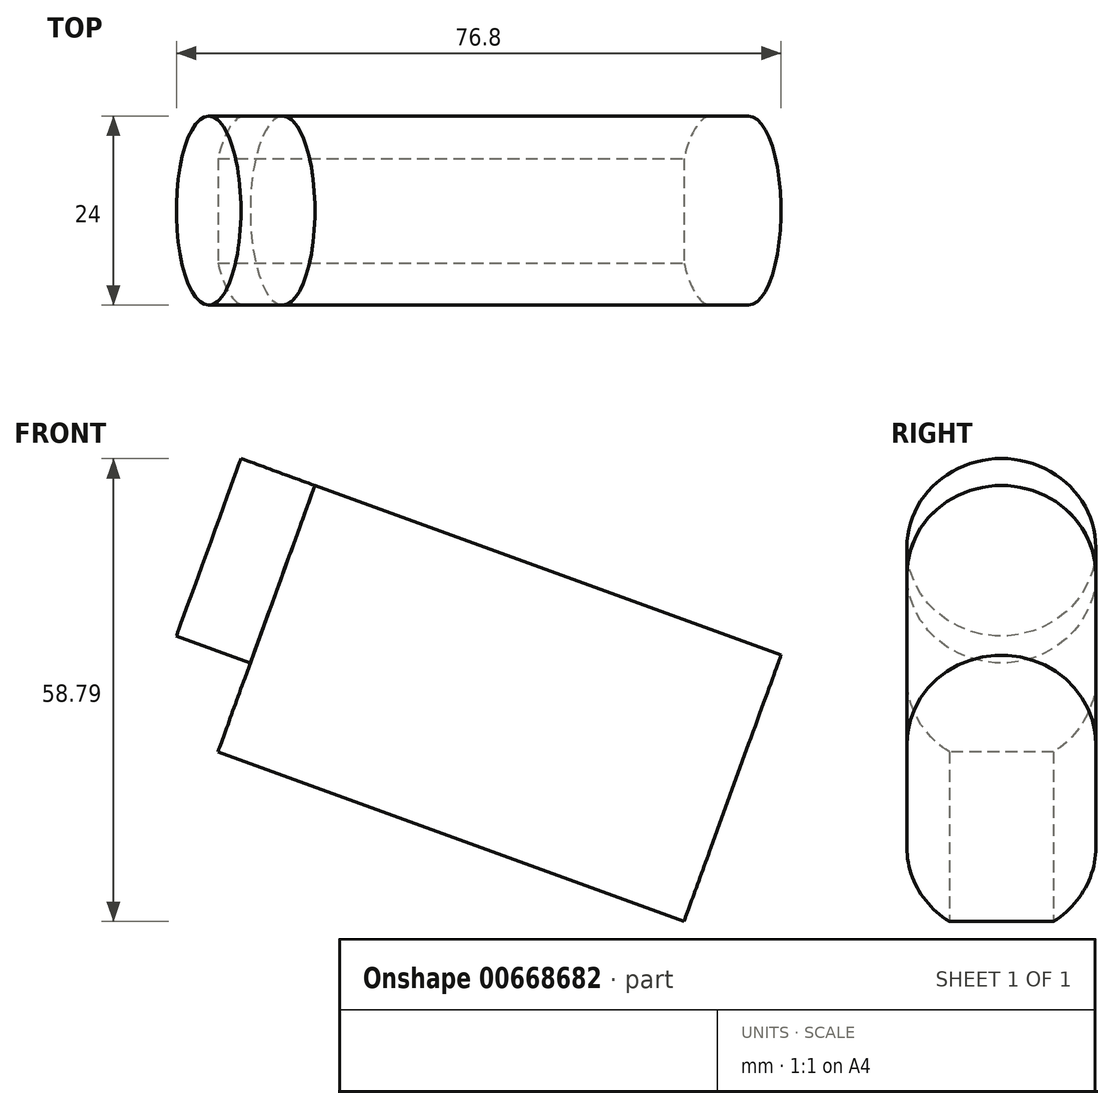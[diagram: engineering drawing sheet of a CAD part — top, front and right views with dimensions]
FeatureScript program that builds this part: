
annotation { "Feature Type Name" : "Feature", "Feature Type Description" : "" }
export const myFeature = defineFeature(function(context is Context, id is Id, definition is map)
    precondition{}
    {
        {
            var Q0;
            Q0=qCreatedBy(makeId("Right.planeOp"),FACE);
            var sketch = newSketch(context, id + "F0", { "sketchPlane" : qUnion([Q0])});
            skLineSegment(sketch, "E0", {"start": v(-93.73, 0) * mm, "end": v(85.96, 0) * mm, "construction": true});
            skSolve(sketch);
        }
        {
            var Q0;
            Q0=qCreatedBy(makeId("Right.planeOp"),FACE);
            var Q1;
            Q1=sQuery(id+"F0.wireOp",EDGE,"E0");
            cPlane(context, id + "F1", {"entities" : qUnion([Q0, Q1]), "cplaneType" : CPlaneType.LINE_ANGLE, "offset" : 25 * mm, "angle" : 20 * degree, "width" : 150 * mm, "height" : 150 * mm});
        }
        {
            var Q0;
            Q0=qCreatedBy(makeId("Top.planeOp"),FACE);
            var sketch = newSketch(context, id + "F2", { "sketchPlane" : qUnion([Q0])});
            skFitSpline(sketch, "E1", {"points": [v(-76, 0) * mm, v(-46.58, 16.57) * mm, v(0, 13) * mm, v(74, 0) * mm], "startDerivative": vector(0.2, 174.07) * mm, "endDerivative": vector(331.92, -62.8) * mm});
            skFitSpline(sketch, "E2.MirrorCS", {"points": [v(-76, 0) * mm, v(-46.58, -16.57) * mm, v(0, -13) * mm, v(74, 0) * mm], "startDerivative": vector(0.2, -174.07) * mm, "endDerivative": vector(331.92, 62.8) * mm});
            skLineSegment(sketch, "E3", {"start": v(-166.1, 0) * mm, "end": v(172.43, 0) * mm, "construction": true});
            skSolve(sketch);
        }
        {
            var Q0;
            Q0=qCreatedBy(id+"F1.planeOp",FACE);
            var sketch = newSketch(context, id + "F3", { "sketchPlane" : qUnion([Q0])});
            skCircle(sketch, "E4", {"center": v(0, 0) * mm, "radius": 12 * mm});
            skArc(sketch, "E5", {"start": v(-12, -14) * mm, "mid": v(-10.57, -19.67) * mm, "end": v(-6.63, -24) * mm});
            skLineSegment(sketch, "E6", {"start": v(-12, 0) * mm, "end": v(-12, -14) * mm});
            skLineSegment(sketch, "E7", {"start": v(12, 0) * mm, "end": v(12, -14) * mm});
            skLineSegment(sketch, "E8", {"start": v(-6.63, -24) * mm, "end": v(6.63, -24) * mm});
            skArc(sketch, "E9.trimOffspring", {"start": v(6.63, -24) * mm, "mid": v(10.57, -19.67) * mm, "end": v(12, -14) * mm});
            skPoint(sketch, "E10", {"position": v(0, 12) * mm});
            skSolve(sketch);
        }
        {
            var Q0;
            {var subQ0=sQuery(id+"F3.wireOp",EDGE,"E4");var subQ1=makeQuery(id+"F3.imprint","INTERSECT",VERTEX,{"derivedFrom":[subQ0,sQuery(id+"F3.wireOp",EDGE,"E6")]});Q0=makeQuery(id+"F3.imprint","IMPRINT",FACE,{"disambiguationData":[TD([[makeQuery(id+"F3.imprint","IMPRINT",EDGE,{"disambiguationData":[TD([[subQ1,-1.0]])],"derivedFrom":subQ0}),1.0]])]});}
            extrude(context, id + "F4", {"entities" : qUnion([Q0]), "depth" : 73 * mm, "offsetDistance" : 25 * mm, "hasSecondDirection" : true, "secondDirectionOppositeDirection" : false, "secondDirectionDepth" : 63 * mm});
        }
        {
            var Q0;
            Q0=makeQuery(id+"F3.imprint","IMPRINT",FACE,{"disambiguationData":[TD([[makeQuery(id+"F3.imprint","IMPRINT",EDGE,{"derivedFrom":sQuery(id+"F3.wireOp",EDGE,"E5")}),1.0]])]});
            var Q1;
            {var subQ0=sQuery(id+"F3.wireOp",EDGE,"E4");var subQ1=makeQuery(id+"F3.imprint","INTERSECT",VERTEX,{"derivedFrom":[subQ0,sQuery(id+"F3.wireOp",EDGE,"E6")]});Q1=makeQuery(id+"F3.imprint","IMPRINT",FACE,{"disambiguationData":[TD([[makeQuery(id+"F3.imprint","IMPRINT",EDGE,{"disambiguationData":[TD([[subQ1,-1.0]])],"derivedFrom":subQ0}),1.0]])]});}
            extrude(context, id + "F5", {"entities" : qUnion([Q0, Q1]), "depth" : 63 * mm, "offsetDistance" : 25 * mm});
        }
        {
            var Q0;
            Q0=sQuery(id+"F2.wireOp",EDGE,"E2.MirrorCS");
            var Q1;
            Q1=sQuery(id+"F2.wireOp",EDGE,"E3");
            revolve(context, id + "F6", {"bodyType" : ToolBodyType.SURFACE, "surfaceOperationType" : NewSurfaceOperationType.NEW, "surfaceEntities" : qUnion([Q0]), "axis" : qUnion([Q1]), "revolveType" : RevolveType.FULL});
        }
    });
